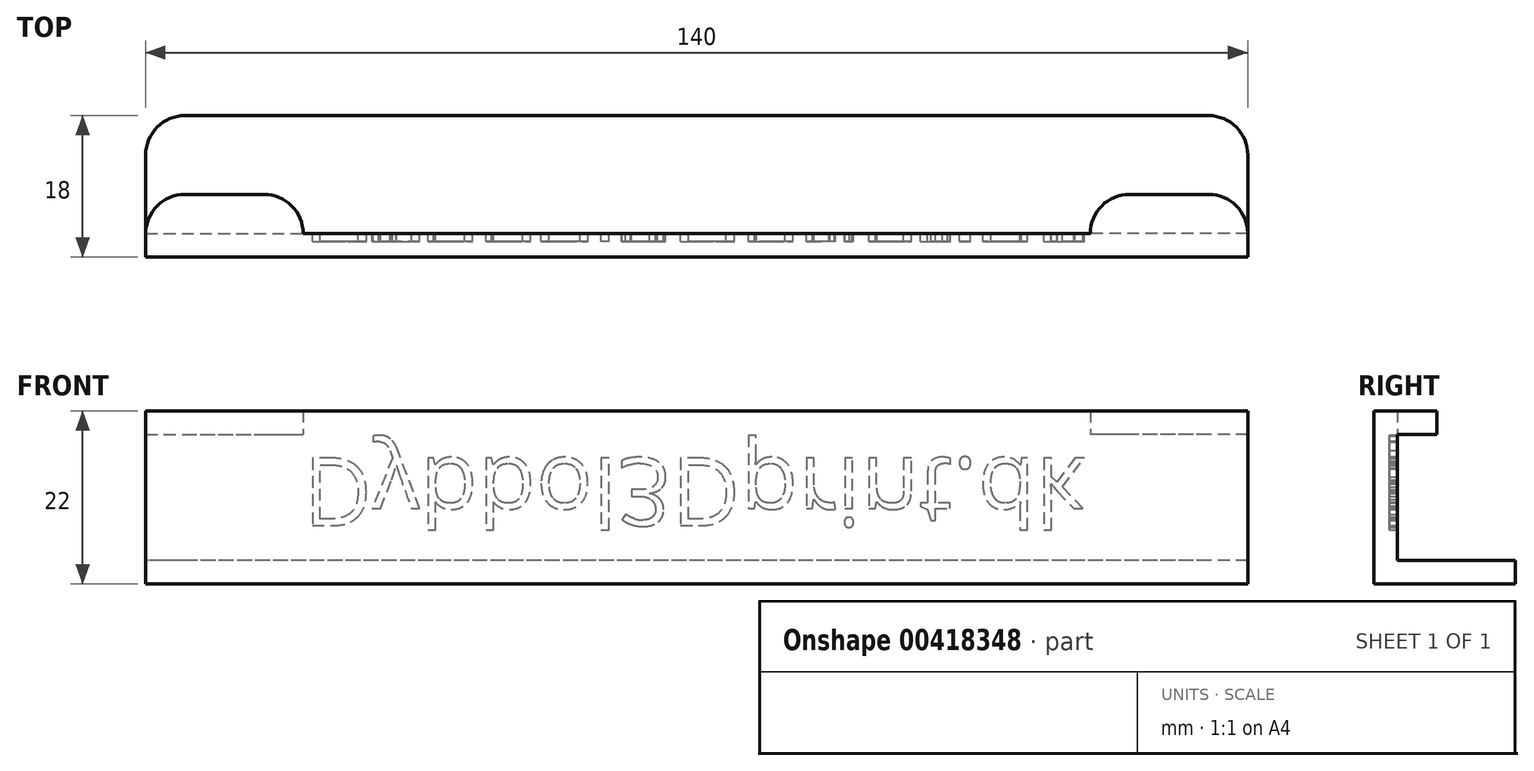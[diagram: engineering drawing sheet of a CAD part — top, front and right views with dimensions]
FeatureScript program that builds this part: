
annotation { "Feature Type Name" : "Feature", "Feature Type Description" : "" }
export const myFeature = defineFeature(function(context is Context, id is Id, definition is map)
    precondition{}
    {
        {
            var Q0;
            Q0=qCreatedBy(makeId("Front.planeOp"),FACE);
            var sketch = newSketch(context, id + "F0", { "sketchPlane" : qUnion([Q0])});
            skLineSegment(sketch, "E0.bottom", {"start": v(-70, 0) * mm, "end": v(70, 0) * mm});
            skLineSegment(sketch, "E0.top", {"start": v(-70, 22) * mm, "end": v(70, 22) * mm});
            skLineSegment(sketch, "E0.left", {"start": v(-70, 0) * mm, "end": v(-70, 22) * mm});
            skLineSegment(sketch, "E0.right", {"start": v(70, 0) * mm, "end": v(70, 22) * mm});
            skSolve(sketch);
        }
        {
            var Q0;
            Q0=makeQuery(id+"F0.imprint","IMPRINT",FACE,{"disambiguationData":[TD([[makeQuery(id+"F0.imprint","IMPRINT",EDGE,{"derivedFrom":sQuery(id+"F0.wireOp",EDGE,"E0.bottom")}),1.0]])]});
            extrude(context, id + "F1", {"entities" : qUnion([Q0]), "depth" : 3 * mm});
        }
        {
            var Q0;
            Q0=makeQuery(id+"F1.opExtrude","CAP_FACE",FACE,{"disambiguationData":[OSD([sQuery(id+"F0.wireOp",EDGE,"E0.bottom"),sQuery(id+"F0.wireOp",EDGE,"E0.top"),sQuery(id+"F0.wireOp",EDGE,"E0.left"),sQuery(id+"F0.wireOp",EDGE,"E0.right")])],"isStart":true});
            var sketch = newSketch(context, id + "F2", { "sketchPlane" : qUnion([Q0])});
            skLineSegment(sketch, "E1.bottom", {"start": v(-70, 0) * mm, "end": v(70, 0) * mm});
            skLineSegment(sketch, "E1.top", {"start": v(-70, 3) * mm, "end": v(70, 3) * mm});
            skLineSegment(sketch, "E1.left", {"start": v(-70, 0) * mm, "end": v(-70, 3) * mm});
            skLineSegment(sketch, "E1.right", {"start": v(70, 0) * mm, "end": v(70, 3) * mm});
            skLineSegment(sketch, "E2.bottom", {"start": v(-70, 22) * mm, "end": v(-50, 22) * mm});
            skLineSegment(sketch, "E2.top", {"start": v(-70, 19) * mm, "end": v(-50, 19) * mm});
            skLineSegment(sketch, "E2.left", {"start": v(-70, 22) * mm, "end": v(-70, 19) * mm});
            skLineSegment(sketch, "E2.right", {"start": v(-50, 22) * mm, "end": v(-50, 19) * mm});
            skPoint(sketch, "E3.oppositeSnap0", {"position": v(-60, 19) * mm});
            skLineSegment(sketch, "E3.bottom", {"start": v(70, 22) * mm, "end": v(50, 22) * mm});
            skLineSegment(sketch, "E3.top", {"start": v(70, 19) * mm, "end": v(50, 19) * mm});
            skLineSegment(sketch, "E3.left", {"start": v(70, 22) * mm, "end": v(70, 19) * mm});
            skLineSegment(sketch, "E3.right", {"start": v(50, 22) * mm, "end": v(50, 19) * mm});
            skSolve(sketch);
        }
        {
            var Q0;
            Q0=makeQuery(id+"F2.imprint","IMPRINT",FACE,{"disambiguationData":[TD([[makeQuery(id+"F2.imprint","IMPRINT",EDGE,{"derivedFrom":sQuery(id+"F2.wireOp",EDGE,"E1.bottom")}),-1.0]])]});
            extrude(context, id + "F3", {"entities" : qUnion([Q0]), "operationType" : NewBodyOperationType.ADD, "depth" : 15 * mm});
        }
        {
            var Q0;
            Q0=makeQuery(id+"F2.imprint","IMPRINT",FACE,{"disambiguationData":[TD([[makeQuery(id+"F2.imprint","IMPRINT",EDGE,{"derivedFrom":sQuery(id+"F2.wireOp",EDGE,"E3.bottom")}),1.0]])]});
            var Q1;
            Q1=makeQuery(id+"F2.imprint","IMPRINT",FACE,{"disambiguationData":[TD([[makeQuery(id+"F2.imprint","IMPRINT",EDGE,{"derivedFrom":sQuery(id+"F2.wireOp",EDGE,"E2.bottom")}),1.0]])]});
            extrude(context, id + "F4", {"entities" : qUnion([Q0, Q1]), "operationType" : NewBodyOperationType.ADD, "depth" : 5 * mm});
        }
        {
            var Q0;
            Q0=makeQuery(id+"F3.opExtrude","CAP_EDGE",EDGE,{"disambiguationData":[OSD([sQuery(id+"F2.wireOp",EDGE,"E1.right")])],"isStart":false});
            var Q1;
            Q1=makeQuery(id+"F3.opExtrude","CAP_EDGE",EDGE,{"disambiguationData":[OSD([sQuery(id+"F2.wireOp",EDGE,"E1.left")])],"isStart":false});
            var Q2;
            Q2=makeQuery(id+"F4.opExtrude","CAP_EDGE",EDGE,{"disambiguationData":[OSD([sQuery(id+"F2.wireOp",EDGE,"E2.left")])],"isStart":false});
            var Q3;
            Q3=makeQuery(id+"F4.opExtrude","CAP_EDGE",EDGE,{"disambiguationData":[OSD([sQuery(id+"F2.wireOp",EDGE,"E2.right")])],"isStart":false});
            var Q4;
            Q4=makeQuery(id+"F4.opExtrude","CAP_EDGE",EDGE,{"disambiguationData":[OSD([sQuery(id+"F2.wireOp",EDGE,"E3.left")])],"isStart":false});
            var Q5;
            Q5=makeQuery(id+"F4.opExtrude","CAP_EDGE",EDGE,{"disambiguationData":[OSD([sQuery(id+"F2.wireOp",EDGE,"E3.right")])],"isStart":false});
            fillet(context, id + "F5", {"entities" : qUnion([Q0, Q1, Q2, Q3, Q4, Q5]), "radius" : 5 * mm, "tangentPropagation" : true, "allowEdgeOverflow" : false});
        }
        {
            var Q0;
            {var subQ3=sQuery(id+"F2.wireOp",EDGE,"E1.top");Q0=makeQuery(id+"F2.imprint","IMPRINT",FACE,{"disambiguationData":[TD([[makeQuery(id+"F2.imprint","IMPRINT",EDGE,{"derivedFrom":subQ3}),1.0]])]});}
            var sketch = newSketch(context, id + "F6", { "sketchPlane" : qUnion([Q0])});
            skText(sketch, "E4", { "text": "Dybbol3Dprint.dk", "fontName": "OpenSans-Regular.ttf"});
            const initialGuessF6  = {"E4": [0.05, 0.016, -1, 0, 0.00866]};
            skSetInitialGuess(sketch, initialGuessF6);
            skSolve(sketch);
        }
        {
            var Q0;
            Q0 = qSketchRegion(id + "F6", true);
            extrude(context, id + "F7", {"entities" : qUnion([Q0]), "operationType" : NewBodyOperationType.REMOVE, "oppositeDirection" : true, "depth" : 1 * mm});
        }
    });
